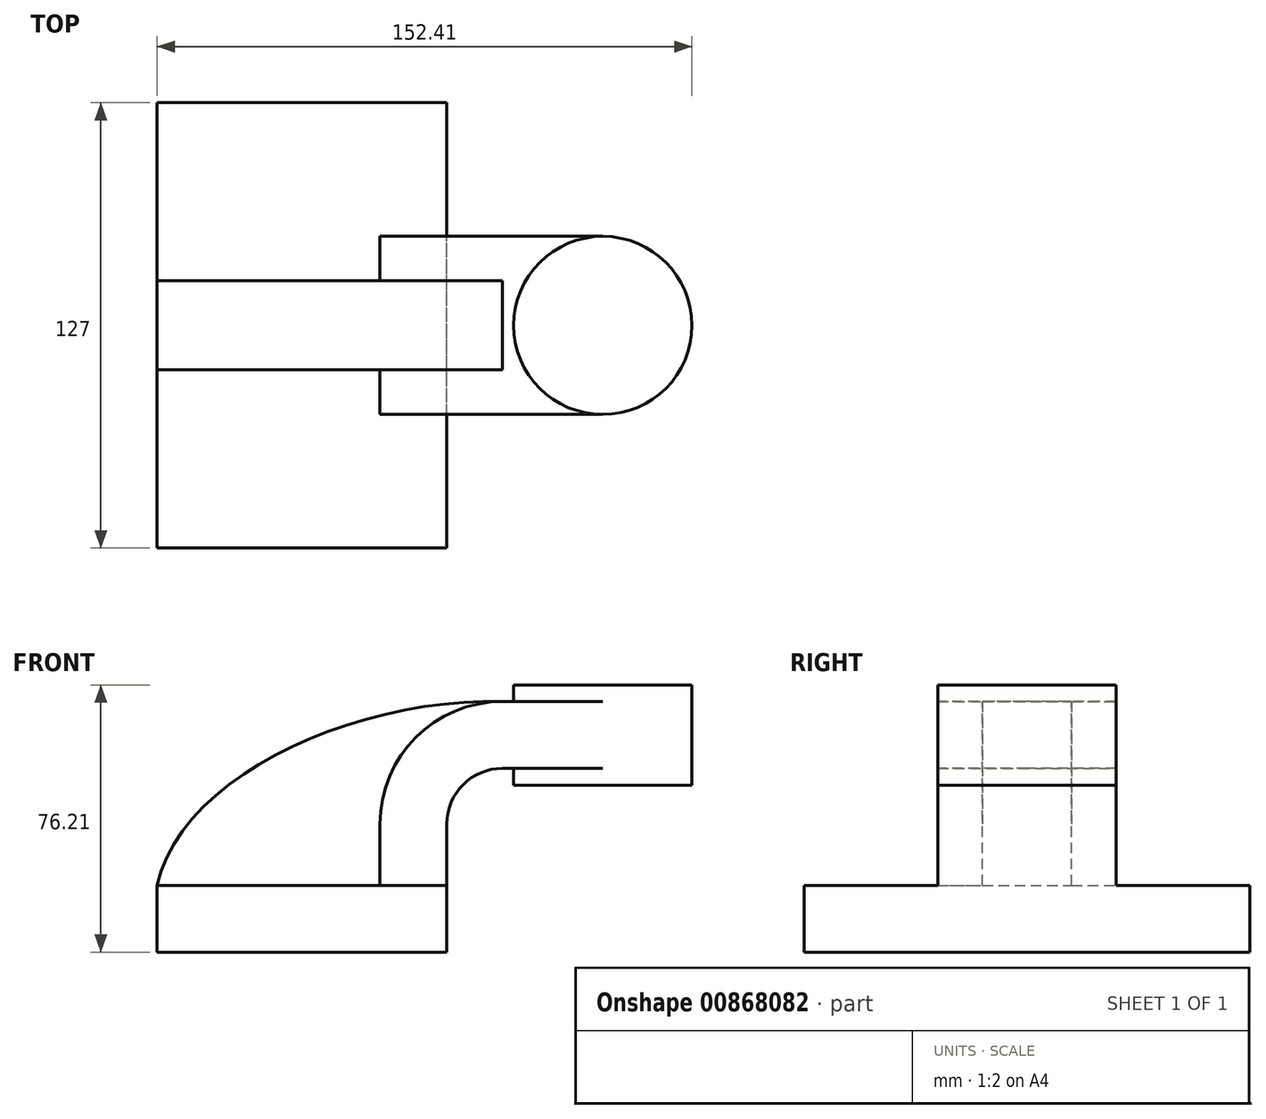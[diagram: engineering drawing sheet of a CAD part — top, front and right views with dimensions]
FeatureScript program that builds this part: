
annotation { "Feature Type Name" : "Feature", "Feature Type Description" : "" }
export const myFeature = defineFeature(function(context is Context, id is Id, definition is map)
    precondition{}
    {
        {
            var Q0;
            Q0=qCreatedBy(makeId("Front.planeOp"),FACE);
            var sketch = newSketch(context, id + "F0", { "sketchPlane" : qUnion([Q0])});
            skLineSegment(sketch, "E0.bottom", {"start": v(-41.28, -9.53) * mm, "end": v(41.28, -9.53) * mm});
            skLineSegment(sketch, "E0.top", {"start": v(-41.28, 9.52) * mm, "end": v(41.27, 9.52) * mm});
            skLineSegment(sketch, "E0.left", {"start": v(-41.27, -9.53) * mm, "end": v(-41.28, 9.52) * mm});
            skLineSegment(sketch, "E0.right", {"start": v(41.28, -9.53) * mm, "end": v(41.27, 9.52) * mm});
            skPoint(sketch, "E0.middle", {"position": v(0, 0) * mm});
            skLineSegment(sketch, "E1.bottom", {"start": v(60.32, 38.1) * mm, "end": v(111.12, 38.1) * mm});
            skLineSegment(sketch, "E1.top", {"start": v(60.32, 66.67) * mm, "end": v(111.12, 66.67) * mm});
            skLineSegment(sketch, "E1.left", {"start": v(60.32, 38.1) * mm, "end": v(60.32, 66.67) * mm});
            skLineSegment(sketch, "E1.right", {"start": v(111.12, 38.1) * mm, "end": v(111.12, 66.67) * mm});
            skPoint(sketch, "E1.middle", {"position": v(85.72, 52.39) * mm});
            skLineSegment(sketch, "E2", {"start": v(41.27, 9.52) * mm, "end": v(41.27, 27) * mm});
            skArc(sketch, "E3", {"start": v(41.27, 27) * mm, "mid": v(45.92, 38.23) * mm, "end": v(57.15, 42.88) * mm});
            skLineSegment(sketch, "E4", {"start": v(57.15, 42.88) * mm, "end": v(85.72, 42.88) * mm});
            skLineSegment(sketch, "E5.0", {"start": v(57.15, 61.93) * mm, "end": v(85.72, 61.93) * mm});
            skArc(sketch, "E5.1", {"start": v(22.22, 27) * mm, "mid": v(32.45, 51.7) * mm, "end": v(57.15, 61.93) * mm});
            skLineSegment(sketch, "E5.2", {"start": v(22.23, 9.52) * mm, "end": v(22.23, 27) * mm});
            skLineSegment(sketch, "E6", {"start": v(22.23, 9.52) * mm, "end": v(41.27, 9.52) * mm});
            skLineSegment(sketch, "E7", {"start": v(85.72, 38.1) * mm, "end": v(85.72, 66.67) * mm});
            skFitSpline(sketch, "E8", {"points": [v(-41.28, 9.53) * mm, v(57.15, 61.93) * mm], "startDerivative": vector(20.37, 93.98) * mm, "endDerivative": vector(125.07, -3.32) * mm});
            skSolve(sketch);
        }
        {
            var Q0;
            Q0=makeQuery(id+"F0.imprint","IMPRINT",FACE,{"disambiguationData":[TD([[makeQuery(id+"F0.imprint","IMPRINT",EDGE,{"derivedFrom":sQuery(id+"F0.wireOp",EDGE,"E0.bottom")}),1.0]])]});
            extrude(context, id + "F1", {"entities" : qUnion([Q0]), "endBound" : BoundingType.SYMMETRIC, "depth" : 127 * mm, "offsetDistance" : 25.4 * mm});
        }
        {
            var Q0;
            Q0=makeQuery(id+"F0.imprint","IMPRINT",FACE,{"disambiguationData":[TD([[makeQuery(id+"F0.imprint","IMPRINT",EDGE,{"derivedFrom":sQuery(id+"F0.wireOp",EDGE,"E2")}),1.0]])]});
            var Q1;
            {var subQ0=sQuery(id+"F0.wireOp",EDGE,"E4");var subQ1=sQuery(id+"F0.wireOp",EDGE,"E1.left");var subQ2=makeQuery(id+"F0.imprint","INTERSECT",VERTEX,{"derivedFrom":[subQ1,subQ0]});Q1=makeQuery(id+"F0.imprint","IMPRINT",FACE,{"disambiguationData":[TD([[makeQuery(id+"F0.imprint","IMPRINT",EDGE,{"disambiguationData":[TD([[subQ2,-1.0]])],"derivedFrom":subQ1}),-1.0]])]});}
            extrude(context, id + "F2", {"entities" : qUnion([Q0, Q1]), "operationType" : NewBodyOperationType.ADD, "endBound" : BoundingType.SYMMETRIC, "depth" : 50.8 * mm, "offsetDistance" : 25.4 * mm});
        }
        {
            var Q0;
            Q0=makeQuery(id+"F0.imprint","IMPRINT",FACE,{"disambiguationData":[TD([[makeQuery(id+"F0.imprint","IMPRINT",EDGE,{"derivedFrom":sQuery(id+"F0.wireOp",EDGE,"E0.top")}),1.0]])]});
            extrude(context, id + "F3", {"entities" : qUnion([Q0]), "operationType" : NewBodyOperationType.ADD, "endBound" : BoundingType.SYMMETRIC, "depth" : 25.4 * mm, "offsetDistance" : 25.4 * mm});
        }
        {
            var Q0;
            {var subQ4=sQuery(id+"F0.wireOp",EDGE,"E1.right");Q0=makeQuery(id+"F0.imprint","IMPRINT",FACE,{"disambiguationData":[TD([[makeQuery(id+"F0.imprint","IMPRINT",EDGE,{"derivedFrom":subQ4}),1.0]])]});}
            var Q1;
            Q1=sQuery(id+"F0.wireOp",EDGE,"E7");
            revolve(context, id + "F4", {"operationType" : NewBodyOperationType.ADD, "surfaceOperationType" : NewSurfaceOperationType.NEW, "entities" : qUnion([Q0]), "axis" : qUnion([Q1]), "revolveType" : RevolveType.FULL});
        }
    });
